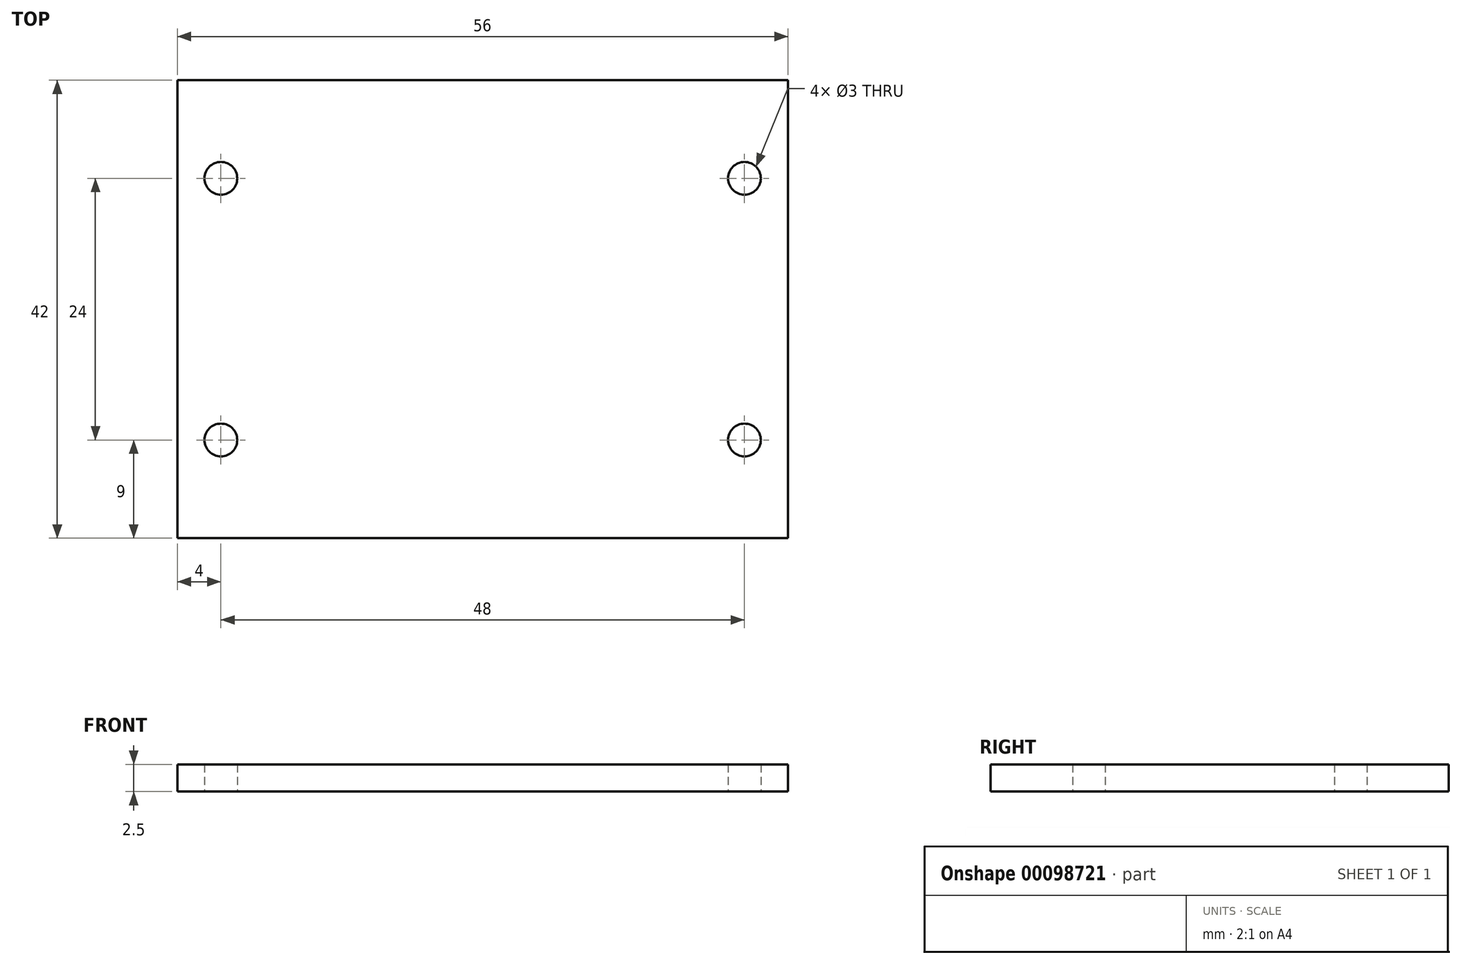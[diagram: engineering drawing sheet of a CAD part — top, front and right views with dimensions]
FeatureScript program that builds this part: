
annotation { "Feature Type Name" : "Feature", "Feature Type Description" : "" }
export const myFeature = defineFeature(function(context is Context, id is Id, definition is map)
    precondition{}
    {
        {
            var Q0;
            Q0=qCreatedBy(makeId("Top.planeOp"),FACE);
            var sketch = newSketch(context, id + "F0", { "sketchPlane" : qUnion([Q0])});
            skLineSegment(sketch, "E0", {"start": v(-28, -21) * mm, "end": v(-28, 21) * mm});
            skLineSegment(sketch, "E1", {"start": v(-28, 21) * mm, "end": v(28, 21) * mm});
            skLineSegment(sketch, "E2", {"start": v(28, 21) * mm, "end": v(28, -21) * mm});
            skLineSegment(sketch, "E3", {"start": v(28, -21) * mm, "end": v(-28, -21) * mm});
            skCircle(sketch, "E4", {"center": v(-24, -12) * mm, "radius": 1.5 * mm});
            skCircle(sketch, "E5", {"center": v(-24, 12) * mm, "radius": 1.5 * mm});
            skCircle(sketch, "E6", {"center": v(24, -12) * mm, "radius": 1.5 * mm});
            skCircle(sketch, "E7", {"center": v(24, 12) * mm, "radius": 1.5 * mm});
            skSolve(sketch);
        }
        {
            var Q0;
            Q0=makeQuery(id+"F0.imprint","IMPRINT",FACE,{"disambiguationData":[TD([[makeQuery(id+"F0.imprint","IMPRINT",EDGE,{"derivedFrom":sQuery(id+"F0.wireOp",EDGE,"E0")}),-1.0]])]});
            extrude(context, id + "F1", {"entities" : qUnion([Q0]), "depth" : 2.5 * mm, "symmetric" : true});
        }
    });
